# Revit family: MEP Björk Hand Dryer
name_source: partatom
category: Electrical Equipment
revit_build: Autodesk Revit 2018 (Build: 20170223_1515(x64)
units: mm (PartAtom-declared; Revit-internal decimal feet)

## family parameters
Always vertical = Yes
Cut with Voids When Loaded = No
Host = Wall
Panel Configuration = Two Columns, Circuits Across
Part Type = Panelboard
Room Calculation Point = No
Round Connector Dimension = Use Diameter
Shared = No

## types (6) — shared parameters
Description = Touch-free hand dryer
Manufacturer = Dan Dryer
Offset from floor = 1100 mm
Type Image = <None>
Voltage = 230
Wattage = Max 1600
zero-valued in all types: Cost

## per-type parameters (varying)
| type | Model | URL |
| BIRK | Björk-3002 | http://www.dandryer.dk |
| GEO WHITE | Björk-3002 | http://www.dandryer.dk |
| GRIGIO LONDRA | Björk-3002 | http://www.dandryer.dk |
| NEGRO INGO | Björk-3002 | http://www.dandryer.dk |
| OSLO | Björk-Serie |  |
| BIANCO MALE | Björk-3002 | http://www.dandryer.com |

## geometry (parser evidence)
native form markers: Sweep x3
no freeform markers — native parametric forms only
